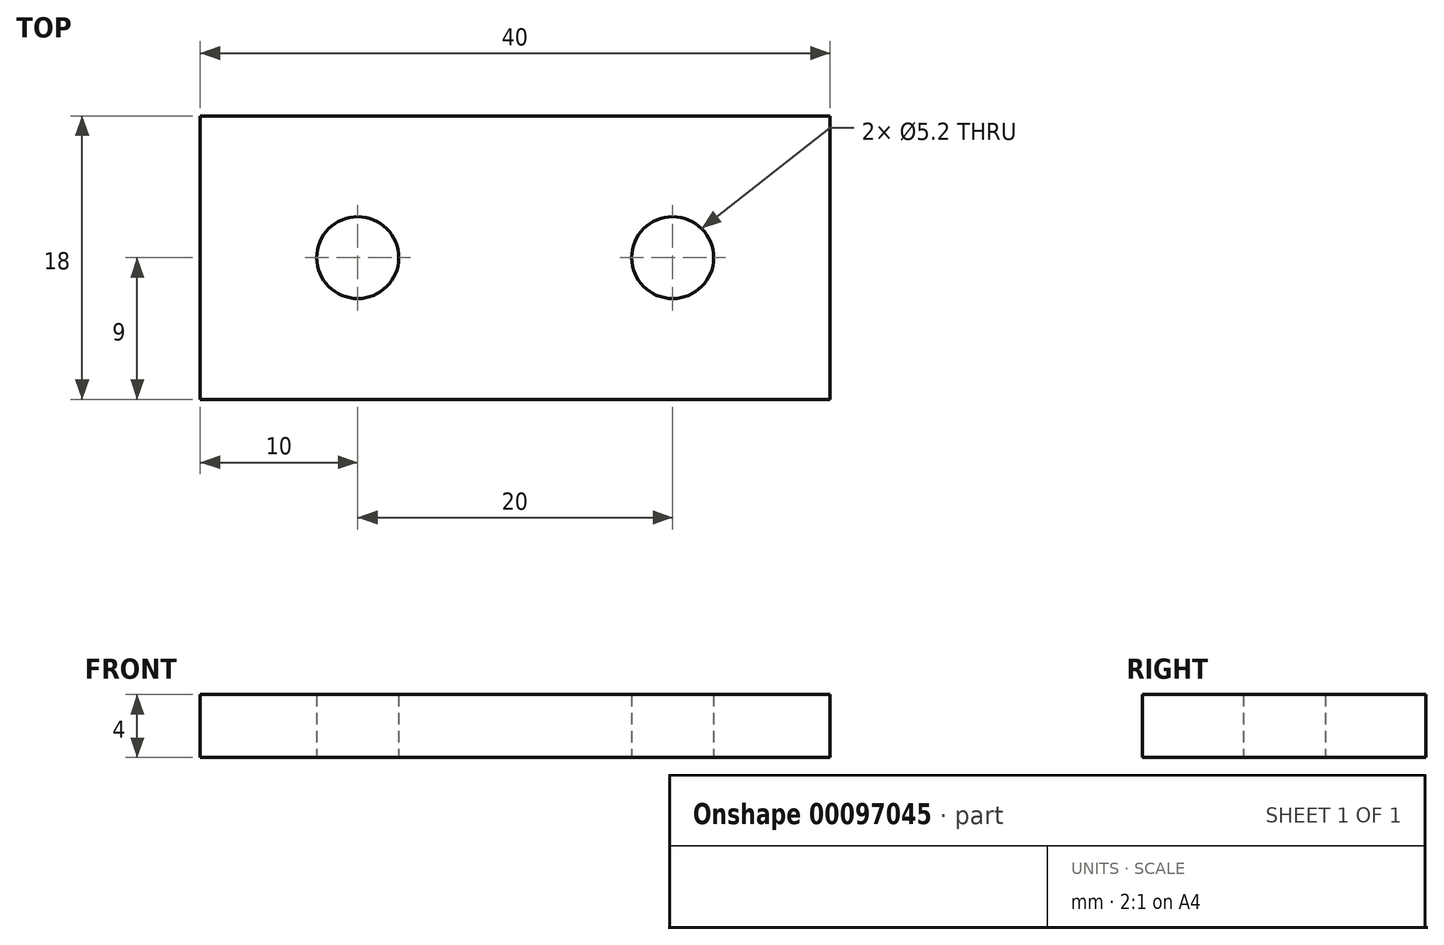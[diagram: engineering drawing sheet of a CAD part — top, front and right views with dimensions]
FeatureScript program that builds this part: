
annotation { "Feature Type Name" : "Feature", "Feature Type Description" : "" }
export const myFeature = defineFeature(function(context is Context, id is Id, definition is map)
    precondition{}
    {
        {
            var Q0;
            Q0=qCreatedBy(makeId("Top.planeOp"),FACE);
            var sketch = newSketch(context, id + "F0", { "sketchPlane" : qUnion([Q0])});
            skLineSegment(sketch, "E0.rect.bottom", {"start": v(20, 9) * mm, "end": v(-20, 9) * mm});
            skLineSegment(sketch, "E0.rect.top", {"start": v(20, -9) * mm, "end": v(-20, -9) * mm});
            skLineSegment(sketch, "E0.rect.left", {"start": v(20, 9) * mm, "end": v(20, -9) * mm});
            skLineSegment(sketch, "E0.rect.right", {"start": v(-20, 9) * mm, "end": v(-20, -9) * mm});
            skPoint(sketch, "E0.rect.middle", {"position": v(0, 0) * mm});
            skCircle(sketch, "E1", {"center": v(10, 0) * mm, "radius": 2.6 * mm});
            skCircle(sketch, "E2", {"center": v(-10, 0) * mm, "radius": 2.6 * mm});
            skSolve(sketch);
        }
        {
            var Q0;
            Q0=qSketchRegion(id+"F0",true);
            extrude(context, id + "F1", {"entities" : qUnion([Q0]), "depth" : 4 * mm});
        }
    });
